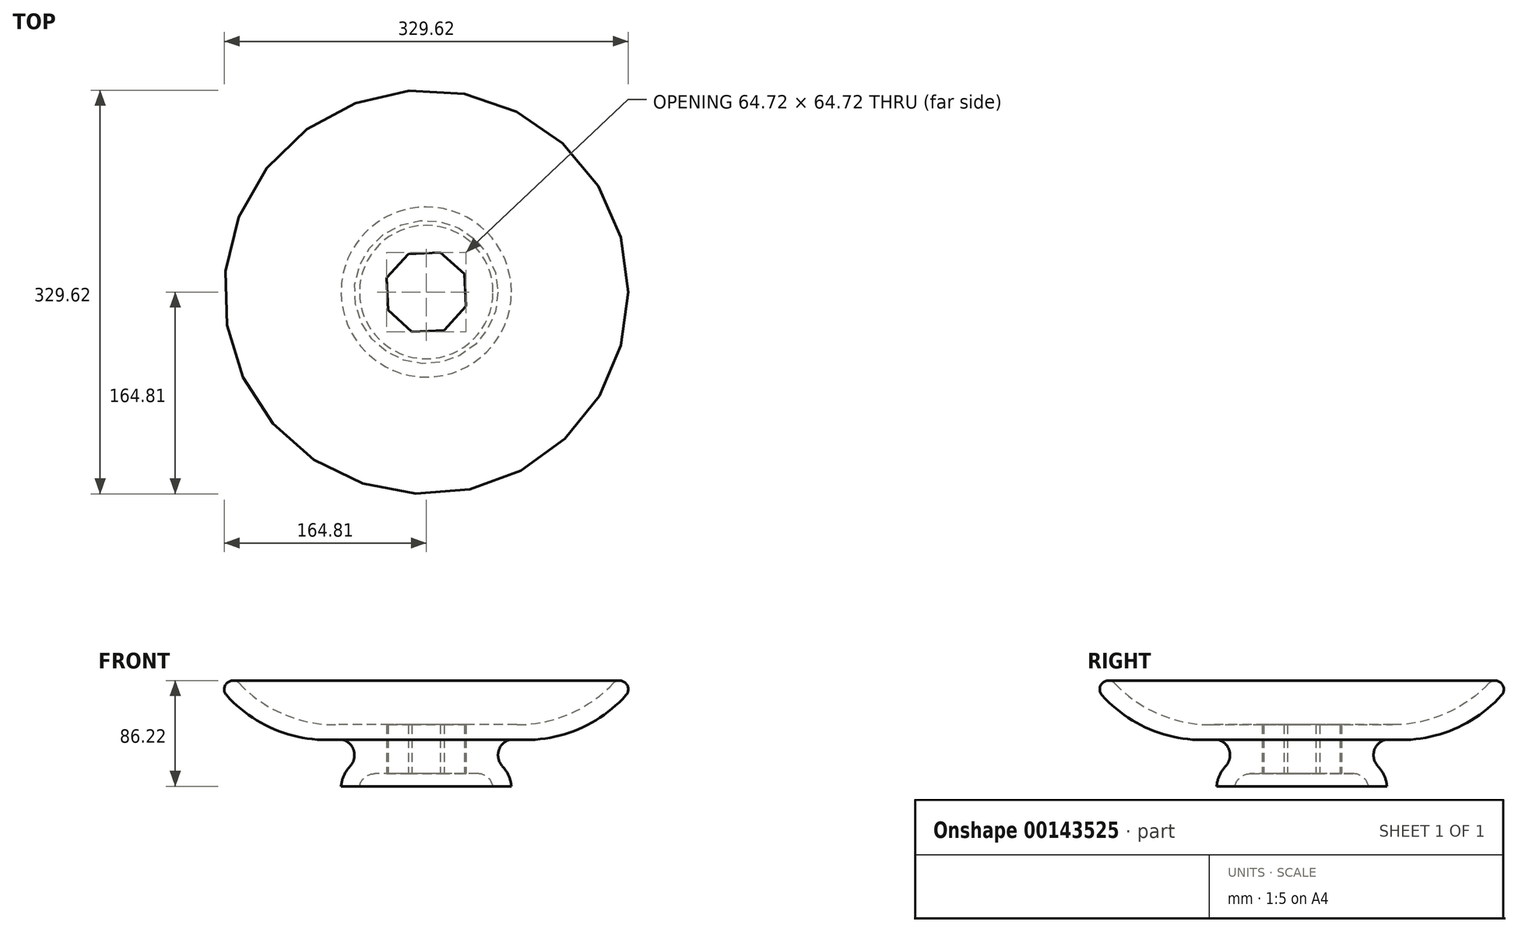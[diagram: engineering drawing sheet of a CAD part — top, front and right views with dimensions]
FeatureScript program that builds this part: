
annotation { "Feature Type Name" : "Feature", "Feature Type Description" : "" }
export const myFeature = defineFeature(function(context is Context, id is Id, definition is map)
    precondition{}
    {
        {
            var Q0;
            Q0=qCreatedBy(makeId("Front.planeOp"),FACE);
            var sketch = newSketch(context, id + "F0", { "sketchPlane" : qUnion([Q0])});
            skLineSegment(sketch, "E0", {"start": v(0, 0) * mm, "end": v(0, 15) * mm});
            skLineSegment(sketch, "E1", {"start": v(0, 0) * mm, "end": v(-42, 0) * mm});
            skArc(sketch, "E2", {"start": v(-42, 0) * mm, "mid": v(-50.07, -2.9) * mm, "end": v(-54.46, -10.25) * mm});
            skLineSegment(sketch, "E3", {"start": v(-54.46, -10.25) * mm, "end": v(-69.46, -10.25) * mm});
            skArc(sketch, "E4", {"start": v(-69.46, -10.25) * mm, "mid": v(-67.17, -1.46) * mm, "end": v(-62.15, 6.12) * mm});
            skArc(sketch, "E5", {"start": v(-62.15, 6.12) * mm, "mid": v(-58.87, 12.4) * mm, "end": v(-59.29, 19.5) * mm});
            skArc(sketch, "E6", {"start": v(-59.29, 19.5) * mm, "mid": v(-64.27, 25.92) * mm, "end": v(-72.15, 27.93) * mm});
            skArc(sketch, "E7", {"start": v(-72.15, 27.93) * mm, "mid": v(-121.8, 35.4) * mm, "end": v(-162.98, 64.1) * mm});
            skArc(sketch, "E8", {"start": v(-162.98, 64.1) * mm, "mid": v(-162.52, 74.09) * mm, "end": v(-152.53, 73.75) * mm});
            skArc(sketch, "E9", {"start": v(-152.53, 73.75) * mm, "mid": v(-116.75, 48.78) * mm, "end": v(-74, 39.97) * mm});
            skLineSegment(sketch, "E10", {"start": v(-74, 39.97) * mm, "end": v(0, 39.97) * mm});
            skLineSegment(sketch, "E11", {"start": v(0, 39.97) * mm, "end": v(0, 15) * mm});
            skSolve(sketch);
        }
        {
            var Q0;
            Q0=makeQuery(id+"F0.imprint","IMPRINT",FACE,{"disambiguationData":[TD([[makeQuery(id+"F0.imprint","IMPRINT",EDGE,{"derivedFrom":sQuery(id+"F0.wireOp",EDGE,"E0")}),1.0]])]});
            var Q1;
            Q1=sQuery(id+"F0.wireOp",EDGE,"E11");
            revolve(context, id + "F1", {"entities" : qUnion([Q0]), "axis" : qUnion([Q1]), "revolveType" : RevolveType.FULL});
        }
        {
            var Q0;
            Q0=makeQuery(id+"F1.opRevolve","SWEPT_FACE",FACE,{"disambiguationData":[OSD([sQuery(id+"F0.wireOp",EDGE,"E3")])]});
            var sketch = newSketch(context, id + "F2", { "sketchPlane" : qUnion([Q0])});
            skCircle(sketch, "E12.cCircle", {"center": v(0, 0) * mm, "radius": 34.37 * mm, "construction": true});
            skLineSegment(sketch, "E12.0", {"start": v(-31.08, 14.69) * mm, "end": v(-11.6, 32.36) * mm});
            skLineSegment(sketch, "E12.1", {"start": v(-11.6, 32.36) * mm, "end": v(14.69, 31.08) * mm});
            skLineSegment(sketch, "E12.2", {"start": v(14.69, 31.08) * mm, "end": v(32.36, 11.6) * mm});
            skLineSegment(sketch, "E12.3", {"start": v(32.36, 11.6) * mm, "end": v(31.08, -14.69) * mm});
            skLineSegment(sketch, "E12.4", {"start": v(31.08, -14.69) * mm, "end": v(11.6, -32.36) * mm});
            skLineSegment(sketch, "E12.5", {"start": v(11.6, -32.36) * mm, "end": v(-14.69, -31.08) * mm});
            skLineSegment(sketch, "E12.6", {"start": v(-14.69, -31.08) * mm, "end": v(-32.36, -11.6) * mm});
            skLineSegment(sketch, "E12.7", {"start": v(-32.36, -11.6) * mm, "end": v(-31.08, 14.69) * mm});
            skLineSegment(sketch, "E13", {"start": v(0, 0) * mm, "end": v(0, -125.26) * mm});
            skSolve(sketch);
        }
        {
            var Q0;
            Q0 = qSketchRegion(id + "F2", true);
            extrude(context, id + "F3", {"entities" : qUnion([Q0]), "operationType" : NewBodyOperationType.REMOVE, "oppositeDirection" : true, "depth" : 70 * mm});
        }
    });
